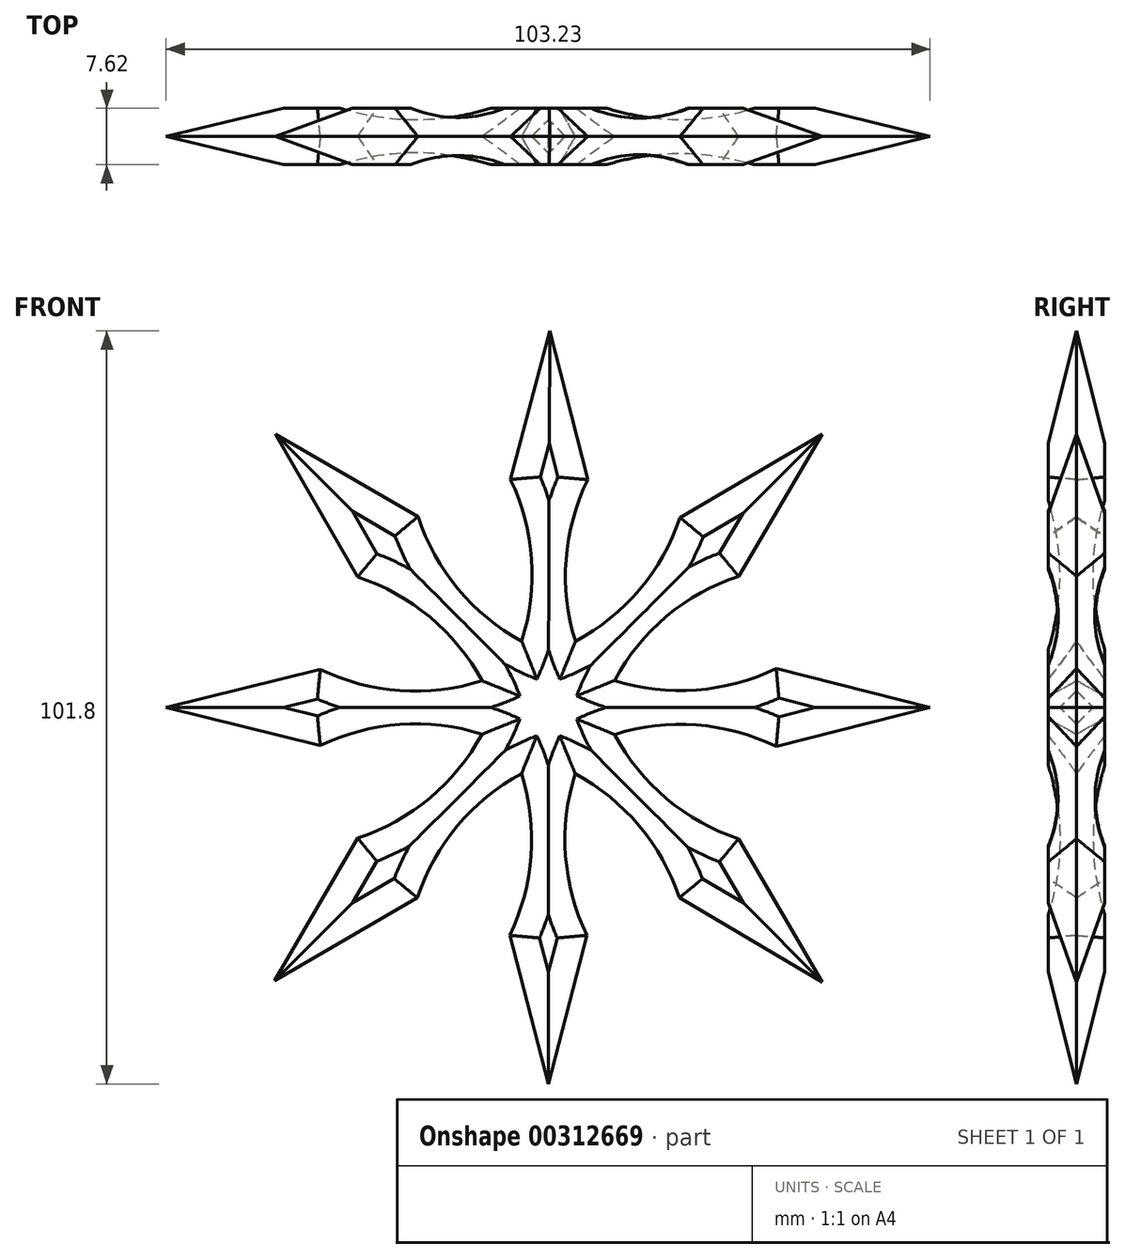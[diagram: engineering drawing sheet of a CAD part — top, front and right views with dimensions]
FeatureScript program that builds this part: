
annotation { "Feature Type Name" : "Feature", "Feature Type Description" : "" }
export const myFeature = defineFeature(function(context is Context, id is Id, definition is map)
    precondition{}
    {
        {
            var Q0;
            Q0=qCreatedBy(makeId("Front.planeOp"),FACE);
            var sketch = newSketch(context, id + "F0", { "sketchPlane" : qUnion([Q0])});
            skPoint(sketch, "E0.0.midPoint", {"position": v(42.7, 24.54) * mm});
            skLineSegment(sketch, "E1", {"start": v(0, 56.78) * mm, "end": v(6.68, 30.64) * mm});
            skArc(sketch, "E2", {"start": v(6.68, 30.64) * mm, "mid": v(3.76, 20.95) * mm, "end": v(4.45, 10.85) * mm});
            skArc(sketch, "E3.MirrorCS", {"start": v(16.74, 26.52) * mm, "mid": v(12.02, 17.57) * mm, "end": v(4.45, 10.85) * mm});
            skArc(sketch, "E4.MirrorCS", {"start": v(26.55, 16.69) * mm, "mid": v(17.6, 11.98) * mm, "end": v(10.86, 4.43) * mm});
            skArc(sketch, "E5.MirrorCS", {"start": v(30.65, 6.62) * mm, "mid": v(20.96, 3.72) * mm, "end": v(10.86, 4.43) * mm});
            skArc(sketch, "E6.MirrorCS", {"start": v(30.65, -6.62) * mm, "mid": v(20.96, -3.72) * mm, "end": v(10.86, -4.43) * mm});
            skArc(sketch, "E7.MirrorCS", {"start": v(26.55, -16.69) * mm, "mid": v(17.6, -11.98) * mm, "end": v(10.86, -4.43) * mm});
            skArc(sketch, "E8.MirrorCS", {"start": v(16.64, -26.58) * mm, "mid": v(11.95, -17.61) * mm, "end": v(4.4, -10.87) * mm});
            skArc(sketch, "E9.MirrorCS", {"start": v(6.57, -30.66) * mm, "mid": v(3.69, -20.96) * mm, "end": v(4.4, -10.87) * mm});
            skLineSegment(sketch, "E10.MirrorCS", {"start": v(-0.21, -56.78) * mm, "end": v(6.57, -30.66) * mm});
            skLineSegment(sketch, "E11.MirrorCS", {"start": v(0.21, -56.78) * mm, "end": v(-6.57, -30.66) * mm});
            skArc(sketch, "E12.MirrorCS", {"start": v(-6.57, -30.66) * mm, "mid": v(-3.69, -20.96) * mm, "end": v(-4.4, -10.87) * mm});
            skArc(sketch, "E13.MirrorCS", {"start": v(-16.64, -26.58) * mm, "mid": v(-11.95, -17.61) * mm, "end": v(-4.4, -10.87) * mm});
            skArc(sketch, "E14.MirrorCS", {"start": v(-26.61, -16.59) * mm, "mid": v(-17.64, -11.92) * mm, "end": v(-10.88, -4.39) * mm});
            skArc(sketch, "E15.MirrorCS", {"start": v(-30.68, -6.5) * mm, "mid": v(-20.97, -3.65) * mm, "end": v(-10.88, -4.39) * mm});
            skArc(sketch, "E16.MirrorCS", {"start": v(-30.68, 6.5) * mm, "mid": v(-20.97, 3.65) * mm, "end": v(-10.88, 4.39) * mm});
            skArc(sketch, "E17.MirrorCS", {"start": v(-26.61, 16.59) * mm, "mid": v(-17.64, 11.92) * mm, "end": v(-10.88, 4.39) * mm});
            skArc(sketch, "E18.MirrorCS", {"start": v(-16.54, 26.64) * mm, "mid": v(-11.88, 17.66) * mm, "end": v(-4.37, 10.89) * mm});
            skArc(sketch, "E19.MirrorCS", {"start": v(-6.45, 30.69) * mm, "mid": v(-3.6, 20.98) * mm, "end": v(-4.37, 10.89) * mm});
            skLineSegment(sketch, "E20.MirrorCS", {"start": v(0.42, 56.78) * mm, "end": v(-6.45, 30.69) * mm});
            skLineSegment(sketch, "E21", {"start": v(-16.64, -26.58) * mm, "end": v(-40.56, -40.48) * mm});
            skLineSegment(sketch, "E22", {"start": v(-26.61, -16.59) * mm, "end": v(-40.56, -40.48) * mm});
            skLineSegment(sketch, "E23", {"start": v(-26.61, 16.59) * mm, "end": v(-40.33, 40.4) * mm});
            skLineSegment(sketch, "E24", {"start": v(-40.33, 40.4) * mm, "end": v(-16.54, 26.64) * mm});
            skLineSegment(sketch, "E25", {"start": v(26.55, 16.69) * mm, "end": v(40.6, 40.52) * mm});
            skLineSegment(sketch, "E26", {"start": v(16.74, 26.52) * mm, "end": v(40.6, 40.52) * mm});
            skLineSegment(sketch, "E27", {"start": v(26.55, -16.69) * mm, "end": v(40.62, -40.7) * mm});
            skLineSegment(sketch, "E28", {"start": v(16.64, -26.58) * mm, "end": v(40.62, -40.7) * mm});
            skLineSegment(sketch, "E29", {"start": v(-30.68, 6.5) * mm, "end": v(-56.93, 0) * mm});
            skLineSegment(sketch, "E30", {"start": v(-30.68, -6.5) * mm, "end": v(-56.93, 0) * mm});
            skLineSegment(sketch, "E31", {"start": v(30.65, -6.62) * mm, "end": v(56.74, 0) * mm});
            skLineSegment(sketch, "E32", {"start": v(30.65, 6.62) * mm, "end": v(56.74, 0) * mm});
            skSolve(sketch);
        }
        {
            var Q0;
            Q0 = qSketchRegion(id + "F0", true);
            extrude(context, id + "F1", {"entities" : qUnion([Q0]), "depth" : 3.8 * mm});
        }
        {
            var Q0;
            Q0=makeQuery(id+"F1.opExtrude","CAP_FACE",FACE,{"disambiguationData":[OSD([sQuery(id+"F0.wireOp",EDGE,"E1"),sQuery(id+"F0.wireOp",EDGE,"E2"),sQuery(id+"F0.wireOp",EDGE,"E3.MirrorCS"),sQuery(id+"F0.wireOp",EDGE,"E4.MirrorCS"),sQuery(id+"F0.wireOp",EDGE,"E5.MirrorCS"),sQuery(id+"F0.wireOp",EDGE,"E6.MirrorCS"),sQuery(id+"F0.wireOp",EDGE,"E7.MirrorCS"),sQuery(id+"F0.wireOp",EDGE,"E8.MirrorCS"),sQuery(id+"F0.wireOp",EDGE,"E9.MirrorCS"),sQuery(id+"F0.wireOp",EDGE,"E10.MirrorCS"),sQuery(id+"F0.wireOp",EDGE,"E11.MirrorCS"),sQuery(id+"F0.wireOp",EDGE,"E12.MirrorCS"),sQuery(id+"F0.wireOp",EDGE,"E13.MirrorCS"),sQuery(id+"F0.wireOp",EDGE,"E14.MirrorCS"),sQuery(id+"F0.wireOp",EDGE,"E15.MirrorCS"),sQuery(id+"F0.wireOp",EDGE,"E16.MirrorCS"),sQuery(id+"F0.wireOp",EDGE,"E17.MirrorCS"),sQuery(id+"F0.wireOp",EDGE,"E18.MirrorCS"),sQuery(id+"F0.wireOp",EDGE,"E19.MirrorCS"),sQuery(id+"F0.wireOp",EDGE,"E20.MirrorCS"),sQuery(id+"F0.wireOp",EDGE,"E21"),sQuery(id+"F0.wireOp",EDGE,"E22"),sQuery(id+"F0.wireOp",EDGE,"E23"),sQuery(id+"F0.wireOp",EDGE,"E24"),sQuery(id+"F0.wireOp",EDGE,"E25"),sQuery(id+"F0.wireOp",EDGE,"E26"),sQuery(id+"F0.wireOp",EDGE,"E27"),sQuery(id+"F0.wireOp",EDGE,"E28"),sQuery(id+"F0.wireOp",EDGE,"E29"),sQuery(id+"F0.wireOp",EDGE,"E30"),sQuery(id+"F0.wireOp",EDGE,"E31"),sQuery(id+"F0.wireOp",EDGE,"E32")])],"isStart":false});
            chamfer(context, id + "F2", {"entities" : qUnion([Q0]), "width" : 5.08 * mm, "tangentPropagation" : true});
        }
        {
            var Q0;
            Q0=makeQuery(id+"F1.opExtrude","SWEPT_BODY",BODY,{"disambiguationData":[OSD([sQuery(id+"F0.wireOp",EDGE,"E1"),sQuery(id+"F0.wireOp",EDGE,"E2"),sQuery(id+"F0.wireOp",EDGE,"E3.MirrorCS"),sQuery(id+"F0.wireOp",EDGE,"E4.MirrorCS"),sQuery(id+"F0.wireOp",EDGE,"E5.MirrorCS"),sQuery(id+"F0.wireOp",EDGE,"E6.MirrorCS"),sQuery(id+"F0.wireOp",EDGE,"E7.MirrorCS"),sQuery(id+"F0.wireOp",EDGE,"E8.MirrorCS"),sQuery(id+"F0.wireOp",EDGE,"E9.MirrorCS"),sQuery(id+"F0.wireOp",EDGE,"E10.MirrorCS"),sQuery(id+"F0.wireOp",EDGE,"E11.MirrorCS"),sQuery(id+"F0.wireOp",EDGE,"E12.MirrorCS"),sQuery(id+"F0.wireOp",EDGE,"E13.MirrorCS"),sQuery(id+"F0.wireOp",EDGE,"E14.MirrorCS"),sQuery(id+"F0.wireOp",EDGE,"E15.MirrorCS"),sQuery(id+"F0.wireOp",EDGE,"E16.MirrorCS"),sQuery(id+"F0.wireOp",EDGE,"E17.MirrorCS"),sQuery(id+"F0.wireOp",EDGE,"E18.MirrorCS"),sQuery(id+"F0.wireOp",EDGE,"E19.MirrorCS"),sQuery(id+"F0.wireOp",EDGE,"E20.MirrorCS"),sQuery(id+"F0.wireOp",EDGE,"E21"),sQuery(id+"F0.wireOp",EDGE,"E22"),sQuery(id+"F0.wireOp",EDGE,"E23"),sQuery(id+"F0.wireOp",EDGE,"E24"),sQuery(id+"F0.wireOp",EDGE,"E25"),sQuery(id+"F0.wireOp",EDGE,"E26"),sQuery(id+"F0.wireOp",EDGE,"E27"),sQuery(id+"F0.wireOp",EDGE,"E28"),sQuery(id+"F0.wireOp",EDGE,"E29"),sQuery(id+"F0.wireOp",EDGE,"E30"),sQuery(id+"F0.wireOp",EDGE,"E31"),sQuery(id+"F0.wireOp",EDGE,"E32")])]});
            var Q1;
            Q1=qCreatedBy(makeId("Front.planeOp"),FACE);
            mirror(context, id + "F3", {"operationType" : NewBodyOperationType.ADD, "entities" : qUnion([Q0]), "mirrorPlane" : qUnion([Q1])});
        }
    });
